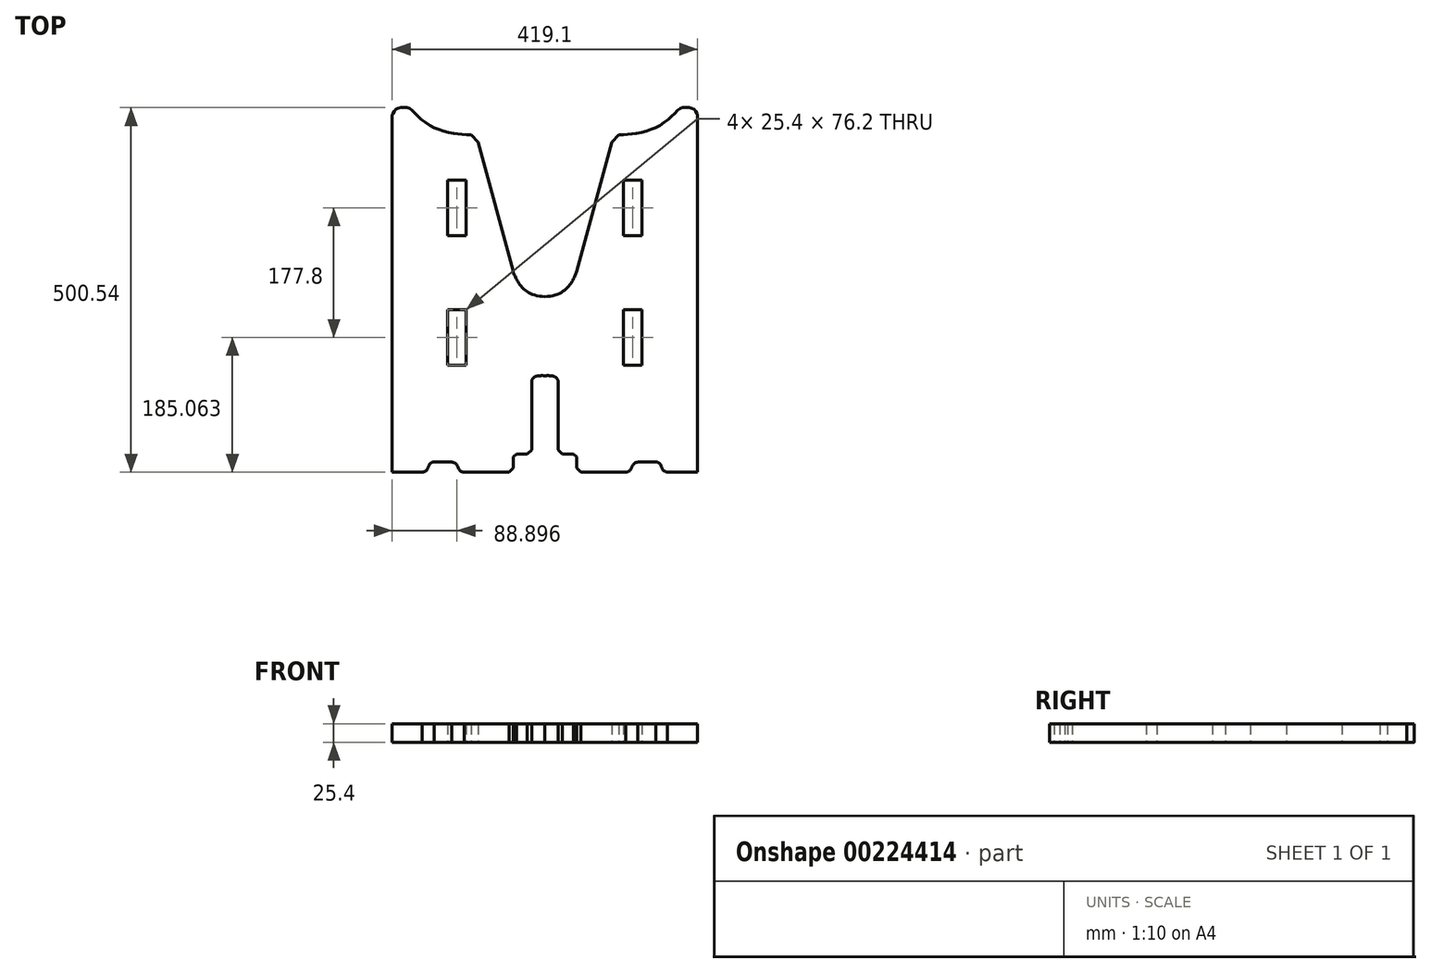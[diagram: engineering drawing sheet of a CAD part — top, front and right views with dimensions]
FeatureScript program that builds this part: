
annotation { "Feature Type Name" : "Feature", "Feature Type Description" : "" }
export const myFeature = defineFeature(function(context is Context, id is Id, definition is map)
    precondition{}
    {
        {
            var Q0;
            Q0=qCreatedBy(makeId("Top.planeOp"),FACE);
            var sketch = newSketch(context, id + "F0", { "sketchPlane" : qUnion([Q0])});
            skLineSegment(sketch, "E0", {"start": v(30.93, 8.46) * mm, "end": v(72.22, 8.46) * mm});
            skLineSegment(sketch, "E1", {"start": v(30.93, 8.46) * mm, "end": v(30.93, 498.32) * mm});
            skFitSpline(sketch, "E2", {"points": [v(30.93, 498.32) * mm, v(31.9, 501.1) * mm, v(33.88, 504.12) * mm, v(36.12, 506.49) * mm, v(39.68, 508.46) * mm, v(45.6, 509) * mm, v(51.66, 508.73) * mm, v(55.74, 507.02) * mm, v(62.6, 500.7) * mm, v(71.54, 492.27) * mm, v(85.5, 483.05) * mm, v(98.14, 477.78) * mm, v(114.73, 473.57) * mm, v(126.72, 472.12) * mm, v(139.1, 471.6) * mm], "startDerivative": vector(17, 69.44) * mm, "endDerivative": vector(143.4, -4.56) * mm});
            skLineSegment(sketch, "E3", {"start": v(139.1, 471.6) * mm, "end": v(148.73, 461.73) * mm});
            skLineSegment(sketch, "E4", {"start": v(148.73, 461.73) * mm, "end": v(196.86, 283.98) * mm});
            skFitSpline(sketch, "E5", {"points": [v(196.86, 283.98) * mm, v(240.48, 249.65) * mm], "startDerivative": vector(10.72, -29.36) * mm, "endDerivative": vector(91.67, 0) * mm});
            skFitSpline(sketch, "E6", {"points": [v(72.22, 8.46) * mm, v(75.81, 9.55) * mm, v(78.19, 11.27) * mm, v(79.78, 13.97) * mm, v(80.64, 16.75) * mm, v(82.11, 19.28) * mm, v(84.11, 21.2) * mm, v(86.36, 22.39) * mm, v(88.32, 22.5) * mm], "startDerivative": vector(26.48, 6.42) * mm, "endDerivative": vector(18.72, -0.75) * mm});
            skLineSegment(sketch, "E7", {"start": v(88.32, 22.5) * mm, "end": v(112.93, 22.5) * mm});
            skFitSpline(sketch, "E8", {"points": [v(112.93, 22.5) * mm, v(115.6, 21.84) * mm, v(117.88, 20.4) * mm, v(119.71, 18.42) * mm, v(121.12, 15.94) * mm, v(122.12, 13.42) * mm, v(124.07, 10.86) * mm, v(126.91, 9.06) * mm, v(129.68, 8.46) * mm], "startDerivative": vector(22.51, -3.96) * mm, "endDerivative": vector(22.37, -3.12) * mm});
            skLineSegment(sketch, "E9", {"start": v(191.14, 8.46) * mm, "end": v(196.94, 14.33) * mm});
            skLineSegment(sketch, "E10", {"start": v(196.94, 14.33) * mm, "end": v(196.94, 29.58) * mm});
            skLineSegment(sketch, "E11", {"start": v(196.94, 29.58) * mm, "end": v(201.45, 33.23) * mm});
            skLineSegment(sketch, "E12", {"start": v(201.45, 33.23) * mm, "end": v(216.28, 33.23) * mm});
            skLineSegment(sketch, "E13", {"start": v(216.28, 33.23) * mm, "end": v(222.18, 39.46) * mm});
            skLineSegment(sketch, "E14", {"start": v(222.18, 39.46) * mm, "end": v(222.18, 133.14) * mm});
            skFitSpline(sketch, "E15", {"points": [v(222.18, 133.14) * mm, v(222.91, 135.65) * mm, v(224.62, 137.88) * mm, v(226.82, 139.64) * mm, v(230.37, 140.81) * mm, v(240.48, 141.08) * mm], "startDerivative": vector(0, 14.5) * mm, "endDerivative": vector(35.86, -0.42) * mm});
            skLineSegment(sketch, "E16.trimOffspring", {"start": v(129.68, 8.46) * mm, "end": v(191.14, 8.46) * mm});
            skPoint(sketch, "E17.trimOffspring.end.orphan", {"position": v(450.03, 8.46) * mm});
            skLineSegment(sketch, "E18.MirrorCS", {"start": v(341.86, 471.6) * mm, "end": v(332.22, 461.73) * mm});
            skFitSpline(sketch, "E19.MirrorCS", {"points": [v(368.02, 22.5) * mm, v(365.34, 21.84) * mm, v(363.08, 20.4) * mm, v(361.24, 18.42) * mm, v(359.84, 15.94) * mm, v(358.83, 13.42) * mm, v(356.88, 10.86) * mm, v(354.04, 9.06) * mm, v(351.27, 8.46) * mm], "startDerivative": vector(-22.51, -3.96) * mm, "endDerivative": vector(-22.37, -3.12) * mm});
            skFitSpline(sketch, "E20.MirrorCS", {"points": [v(408.74, 8.46) * mm, v(405.14, 9.55) * mm, v(402.77, 11.27) * mm, v(401.17, 13.97) * mm, v(400.31, 16.75) * mm, v(398.84, 19.28) * mm, v(396.84, 21.2) * mm, v(394.6, 22.39) * mm, v(392.63, 22.5) * mm], "startDerivative": vector(-26.48, 6.42) * mm, "endDerivative": vector(-18.72, -0.75) * mm});
            skLineSegment(sketch, "E21.MirrorCS", {"start": v(392.63, 22.5) * mm, "end": v(368.02, 22.5) * mm});
            skLineSegment(sketch, "E22.MirrorCS", {"start": v(289.81, 8.46) * mm, "end": v(284.01, 14.33) * mm});
            skLineSegment(sketch, "E23.MirrorCS", {"start": v(284.01, 14.33) * mm, "end": v(284.01, 29.58) * mm});
            skFitSpline(sketch, "E24.MirrorCS", {"points": [v(258.77, 133.14) * mm, v(258.04, 135.65) * mm, v(256.34, 137.88) * mm, v(254.14, 139.64) * mm, v(250.59, 140.81) * mm, v(240.48, 141.08) * mm], "startDerivative": vector(0, 14.5) * mm, "endDerivative": vector(-35.86, -0.42) * mm});
            skLineSegment(sketch, "E25.MirrorCS", {"start": v(279.5, 33.23) * mm, "end": v(264.68, 33.23) * mm});
            skLineSegment(sketch, "E26.MirrorCS", {"start": v(264.68, 33.23) * mm, "end": v(258.77, 39.46) * mm});
            skLineSegment(sketch, "E27.MirrorCS", {"start": v(284.01, 29.58) * mm, "end": v(279.5, 33.23) * mm});
            skFitSpline(sketch, "E28.MirrorCS", {"points": [v(450.03, 498.32) * mm, v(449.04, 501.1) * mm, v(447.07, 504.12) * mm, v(444.83, 506.49) * mm, v(441.27, 508.46) * mm, v(435.35, 509) * mm, v(429.3, 508.73) * mm, v(425.2, 507.02) * mm, v(418.36, 500.7) * mm, v(409.4, 492.27) * mm, v(395.45, 483.05) * mm, v(382.8, 477.78) * mm, v(366.22, 473.57) * mm, v(354.24, 472.12) * mm, v(341.86, 471.6) * mm], "startDerivative": vector(-17, 69.44) * mm, "endDerivative": vector(-143.4, -4.56) * mm});
            skFitSpline(sketch, "E29.MirrorCS", {"points": [v(284.1, 283.98) * mm, v(240.48, 249.65) * mm], "startDerivative": vector(-10.72, -29.36) * mm, "endDerivative": vector(-91.67, 0) * mm});
            skLineSegment(sketch, "E30.MirrorCS", {"start": v(450.03, 8.46) * mm, "end": v(408.74, 8.46) * mm});
            skLineSegment(sketch, "E31.MirrorCS", {"start": v(332.22, 461.73) * mm, "end": v(284.1, 283.98) * mm});
            skLineSegment(sketch, "E32.MirrorCS", {"start": v(351.27, 8.46) * mm, "end": v(289.81, 8.46) * mm});
            skLineSegment(sketch, "E33.MirrorCS", {"start": v(450.03, 8.46) * mm, "end": v(450.03, 498.32) * mm});
            skLineSegment(sketch, "E34.MirrorCS", {"start": v(258.77, 39.46) * mm, "end": v(258.77, 133.14) * mm});
            skLineSegment(sketch, "E35.bottom", {"start": v(132.53, 409.42) * mm, "end": v(107.13, 409.42) * mm});
            skLineSegment(sketch, "E35.top", {"start": v(132.53, 333.22) * mm, "end": v(107.13, 333.22) * mm});
            skLineSegment(sketch, "E35.left", {"start": v(132.53, 409.42) * mm, "end": v(132.53, 333.22) * mm});
            skLineSegment(sketch, "E35.right", {"start": v(107.13, 409.42) * mm, "end": v(107.13, 333.22) * mm});
            skPoint(sketch, "E35.middle", {"position": v(119.83, 371.32) * mm});
            skLineSegment(sketch, "E36.bottom", {"start": v(132.53, 231.62) * mm, "end": v(107.13, 231.62) * mm});
            skLineSegment(sketch, "E36.top", {"start": v(132.53, 155.42) * mm, "end": v(107.13, 155.42) * mm});
            skLineSegment(sketch, "E36.left", {"start": v(132.53, 231.62) * mm, "end": v(132.53, 155.42) * mm});
            skLineSegment(sketch, "E36.right", {"start": v(107.13, 231.62) * mm, "end": v(107.13, 155.42) * mm});
            skPoint(sketch, "E36.middle", {"position": v(119.83, 193.52) * mm});
            skPoint(sketch, "E36.middle.positionSnap0", {"position": v(119.83, 333.22) * mm});
            skPoint(sketch, "E36.centerSnap0", {"position": v(119.83, 333.22) * mm});
            skLineSegment(sketch, "E37.MirrorCS", {"start": v(348.43, 333.22) * mm, "end": v(373.83, 333.22) * mm});
            skPoint(sketch, "E38.MirrorP", {"position": v(361.13, 333.22) * mm});
            skLineSegment(sketch, "E39.MirrorCS", {"start": v(373.83, 231.62) * mm, "end": v(373.83, 155.42) * mm});
            skPoint(sketch, "E40.MirrorP", {"position": v(361.13, 371.32) * mm});
            skPoint(sketch, "E41.MirrorP", {"position": v(361.13, 193.52) * mm});
            skLineSegment(sketch, "E42.MirrorCS", {"start": v(348.43, 409.42) * mm, "end": v(348.43, 333.22) * mm});
            skLineSegment(sketch, "E43.MirrorCS", {"start": v(373.83, 409.42) * mm, "end": v(373.83, 333.22) * mm});
            skLineSegment(sketch, "E44.MirrorCS", {"start": v(348.43, 231.62) * mm, "end": v(373.83, 231.62) * mm});
            skLineSegment(sketch, "E45.MirrorCS", {"start": v(348.43, 155.42) * mm, "end": v(373.83, 155.42) * mm});
            skLineSegment(sketch, "E46.MirrorCS", {"start": v(348.43, 409.42) * mm, "end": v(373.83, 409.42) * mm});
            skLineSegment(sketch, "E47.MirrorCS", {"start": v(348.43, 231.62) * mm, "end": v(348.43, 155.42) * mm});
            skSolve(sketch);
        }
        {
            var Q0;
            Q0 = qSketchRegion(id + "F0", true);
            extrude(context, id + "F1", {"entities" : qUnion([Q0]), "depth" : 25.4 * mm});
        }
    });
